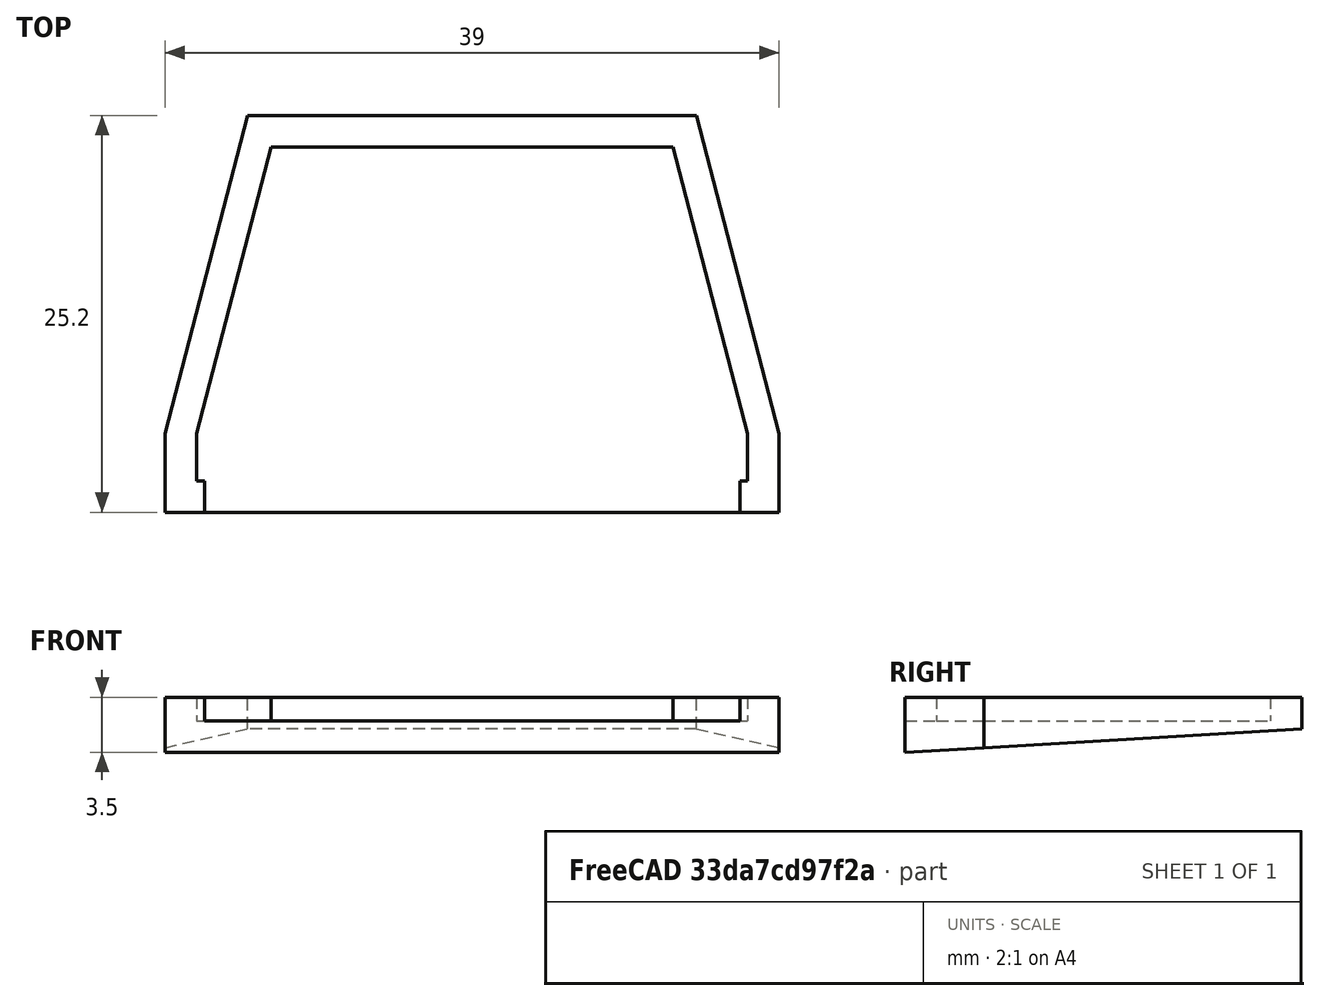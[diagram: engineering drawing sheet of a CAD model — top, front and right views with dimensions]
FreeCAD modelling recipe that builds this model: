
FCSTD DOCUMENT  (FreeCAD 0.17R13541 (Git))
Label: Sample block
License: All rights reserved
LicenseURL: http://en.wikipedia.org/wiki/All_rights_reserved
objects: Sketcher::SketchObject×3, PartDesign::Pocket×2, PartDesign::Pad×1, PartDesign::Body×1, Mesh::Feature×1
note: 10 computed .brp shape members not serialized (recipe doc carries the construction recipe); baked Part::Feature solids carry a one-line shape summary decoded from their .brp

FEATURE [Sketcher::SketchObject] Sketch
  MapMode = 5
  Support = -> [XY_Plane]
  expr: Constraints[27] = 14.199999999999999mm - 9.5mm
  sketch-geometry (18):
    g0: LineSegment [constr] StartX=-11.75 StartY=14.2 StartZ=0 EndX=11.75 EndY=14.2 EndZ=0
    g1: LineSegment [constr] StartX=11.75 StartY=14.2 StartZ=0 EndX=11.75 EndY=4.7 EndZ=0
    g2: LineSegment [constr] StartX=11.75 StartY=4.7 StartZ=0 EndX=-11.75 EndY=4.7 EndZ=0
    g3: LineSegment [constr] StartX=-11.75 StartY=4.7 StartZ=0 EndX=-11.75 EndY=14.2 EndZ=0
    g4: LineSegment [constr] StartX=-10.25 StartY=4.7 StartZ=0 EndX=10.25 EndY=4.7 EndZ=0
    g5: LineSegment [constr] StartX=10.25 StartY=4.7 StartZ=0 EndX=10.25 EndY=0 EndZ=0
    g6: LineSegment [constr] StartX=10.25 StartY=0 StartZ=0 EndX=-10.25 EndY=0 EndZ=0
    g7: LineSegment [constr] StartX=-10.25 StartY=0 StartZ=0 EndX=-10.25 EndY=4.7 EndZ=0
    g8: LineSegment [constr] StartX=-17 StartY=-6 StartZ=0 EndX=17 EndY=-6 EndZ=0
    g9: LineSegment [constr] StartX=17 StartY=-6 StartZ=0 EndX=17 EndY=-8.5 EndZ=0
    g10: LineSegment [constr] StartX=17 StartY=-8.5 StartZ=0 EndX=-17 EndY=-8.5 EndZ=0
    g11: LineSegment [constr] StartX=-17 StartY=-8.5 StartZ=0 EndX=-17 EndY=-6 EndZ=0
    g12: LineSegment StartX=-19.5 StartY=-8.5 StartZ=0 EndX=-19.5 EndY=-3.5 EndZ=0
    g13: LineSegment StartX=-14.25 StartY=16.7 StartZ=0 EndX=14.25 EndY=16.7 EndZ=0
    g14: LineSegment StartX=-14.25 StartY=16.7 StartZ=0 EndX=-19.5 EndY=-3.5 EndZ=0
    g15: LineSegment StartX=-19.5 StartY=-8.5 StartZ=0 EndX=19.5 EndY=-8.5 EndZ=0
    g16: LineSegment StartX=19.5 StartY=-8.5 StartZ=0 EndX=19.5 EndY=-3.5 EndZ=0
    g17: LineSegment StartX=19.5 StartY=-3.5 StartZ=0 EndX=14.25 EndY=16.7 EndZ=0
  constraints (53):
    c: Coincident(g0,g1)
    c: Coincident(g1,g2)
    c: Coincident(g2,g3)
    c: Coincident(g3,g0)
    c: Horizontal(g0)
    c: Horizontal(g2)
    c: Vertical(g1)
    c: Vertical(g3)
    c: Coincident(g4,g5)
    c: Coincident(g5,g6)
    c: Coincident(g6,g7)
    c: Coincident(g7,g4)
    c: Horizontal(g4)
    c: Horizontal(g6)
    c: Vertical(g5)
    c: Vertical(g7)
    c: PointOnObject(g4,g2)
    c: Coincident(g8,g9)
    c: Coincident(g9,g10)
    c: Coincident(g10,g11)
    c: Coincident(g11,g8)
    c: Horizontal(g8)
    c: Horizontal(g10)
    c: Vertical(g9)
    c: Vertical(g11)
    c: Distance(g0) = 23.5
    c: Distance(g1) = 9.5
    c: Distance(g5) = 4.7
    c: Distance(g6) = 20.5
    c: Distance(g10) = 34
    c: Distance(g9) = 2.5
    c: Symmetric(g0,g0,g-2)
    c: Symmetric(g5,g6,g-2)
    c: Symmetric(g8,g8,g-2)
    c: PointOnObject(g-1,g6)
    c: DistanceY(g8,g5) = 6
    c: Vertical(g12)
    c: Horizontal(g13)
    c: Coincident(g14,g13)
    c: Coincident(g14,g12)
    c: Coincident(g15,g12)
    c: Horizontal(g15)
    c: Coincident(g16,g15)
    c: Vertical(g16)
    c: Coincident(g17,g16)
    c: Coincident(g17,g13)
    c: PointOnObject(g10,g15)
    c: Symmetric(g12,g16,g-2)
    c: Symmetric(g13,g13,g-2)
    c: DistanceX(g12,g10) = 2.5
    c: DistanceY(g8,g12) = 2.5
    c: DistanceY(g0,g13) = 2.5
    c: DistanceX(g13,g0) = 2.5
FEATURE [PartDesign::Pad] Pad
  Length = 3.5
  Length2 = 100
  Profile = -> Sketch
  Type = 0
FEATURE [Sketcher::SketchObject] Sketch001
  ExternalGeometry = -> [Pad]
  MapMode = 5
  Placement = pos=(0,0,3.5) rot=(0,0,1;0rad)
  Support = -> [Pad]
  sketch-geometry (10):
    g0: LineSegment StartX=-12.7698 StartY=14.7 StartZ=0 EndX=12.7698 EndY=14.7 EndZ=0
    g1: LineSegment StartX=12.7698 StartY=14.7 StartZ=0 EndX=17.5 EndY=-3.5 EndZ=0
    g2: LineSegment StartX=17.5 StartY=-3.5 StartZ=0 EndX=17.5 EndY=-6.5 EndZ=0
    g3: LineSegment StartX=-17.5 StartY=-6.5 StartZ=0 EndX=-17.5 EndY=-3.5 EndZ=0
    g4: LineSegment StartX=-17.5 StartY=-3.5 StartZ=0 EndX=-12.7698 EndY=14.7 EndZ=0
    g5: LineSegment StartX=17 StartY=-6.5 StartZ=0 EndX=17 EndY=-8.5 EndZ=0
    g6: LineSegment StartX=17 StartY=-8.5 StartZ=0 EndX=-17 EndY=-8.5 EndZ=0
    g7: LineSegment StartX=-17 StartY=-8.5 StartZ=0 EndX=-17 EndY=-6.5 EndZ=0
    g8: LineSegment StartX=-17.5 StartY=-6.5 StartZ=0 EndX=-17 EndY=-6.5 EndZ=0
    g9: LineSegment StartX=17 StartY=-6.5 StartZ=0 EndX=17.5 EndY=-6.5 EndZ=0
  constraints (29):
    c: Horizontal(g0)
    c: Coincident(g1,g0)
    c: Coincident(g2,g1)
    c: Vertical(g2)
    c: Vertical(g3)
    c: Coincident(g4,g0)
    c: Symmetric(g3,g1,g-2)
    c: Coincident(g3,g4)
    c: Symmetric(g0,g0,g-2)
    c: DistanceY(g-8,g3) = 2
    c: DistanceX(g-8,g3) = 2
    c: DistanceY(g0,g-7) = 2
    c: Parallel(g4,g-7)
    c: Horizontal(g-8,g3)
    c: Coincident(g5,g6)
    c: Coincident(g6,g7)
    c: Horizontal(g6)
    c: Vertical(g5)
    c: Vertical(g7)
    c: PointOnObject(g5,g-6)
    c: Symmetric(g6,g5,g-2)
    c: Distance(g6) = 34
    c: Coincident(g8,g3)
    c: Coincident(g8,g7)
    c: Horizontal(g8)
    c: Coincident(g9,g5)
    c: Coincident(g9,g2)
    c: Horizontal(g9)
    c: Horizontal(g5,g7)
FEATURE [PartDesign::Pocket] Pocket
  BaseFeature = -> Pad
  Length = 1.5
  Length2 = 100
  Profile = -> Sketch001
  Type = 0
FEATURE [Sketcher::SketchObject] Sketch002
  ExternalGeometry = -> [Pocket]
  MapMode = 5
  Placement = pos=(19.5,0,0) rot=(0.57735,0.57735,0.57735;2.0944rad)
  Support = -> [Pocket]
  sketch-geometry (3):
    g0: LineSegment StartX=-8.5 StartY=0 StartZ=0 EndX=16.7 EndY=1.5 EndZ=0
    g1: LineSegment StartX=16.7 StartY=1.5 StartZ=0 EndX=16.7 EndY=0 EndZ=0
    g2: LineSegment StartX=16.7 StartY=0 StartZ=0 EndX=-8.5 EndY=0 EndZ=0
  constraints (8):
    c: Vertical(g1)
    c: Coincident(g2,g1)
    c: Coincident(g2,g0)
    c: Horizontal(g2)
    c: PointOnObject(g0,g-3)
    c: Distance(g0,g-3) = 2
    c: Coincident(g0,g-4)
    c: Coincident(g1,g0)
FEATURE [PartDesign::Pocket] Pocket001
  BaseFeature = -> Pocket
  Length = 5
  Length2 = 100
  Profile = -> Sketch002
  Type = 1
FEATURE [PartDesign::Body] Body
  Group = -> [Sketch,Pad,Sketch001,Pocket,Sketch002,Pocket001]
  Origin = -> Origin
  Tip = -> Pocket001
FEATURE [Mesh::Feature] Mesh  label="Pocket001 (Meshed)"
